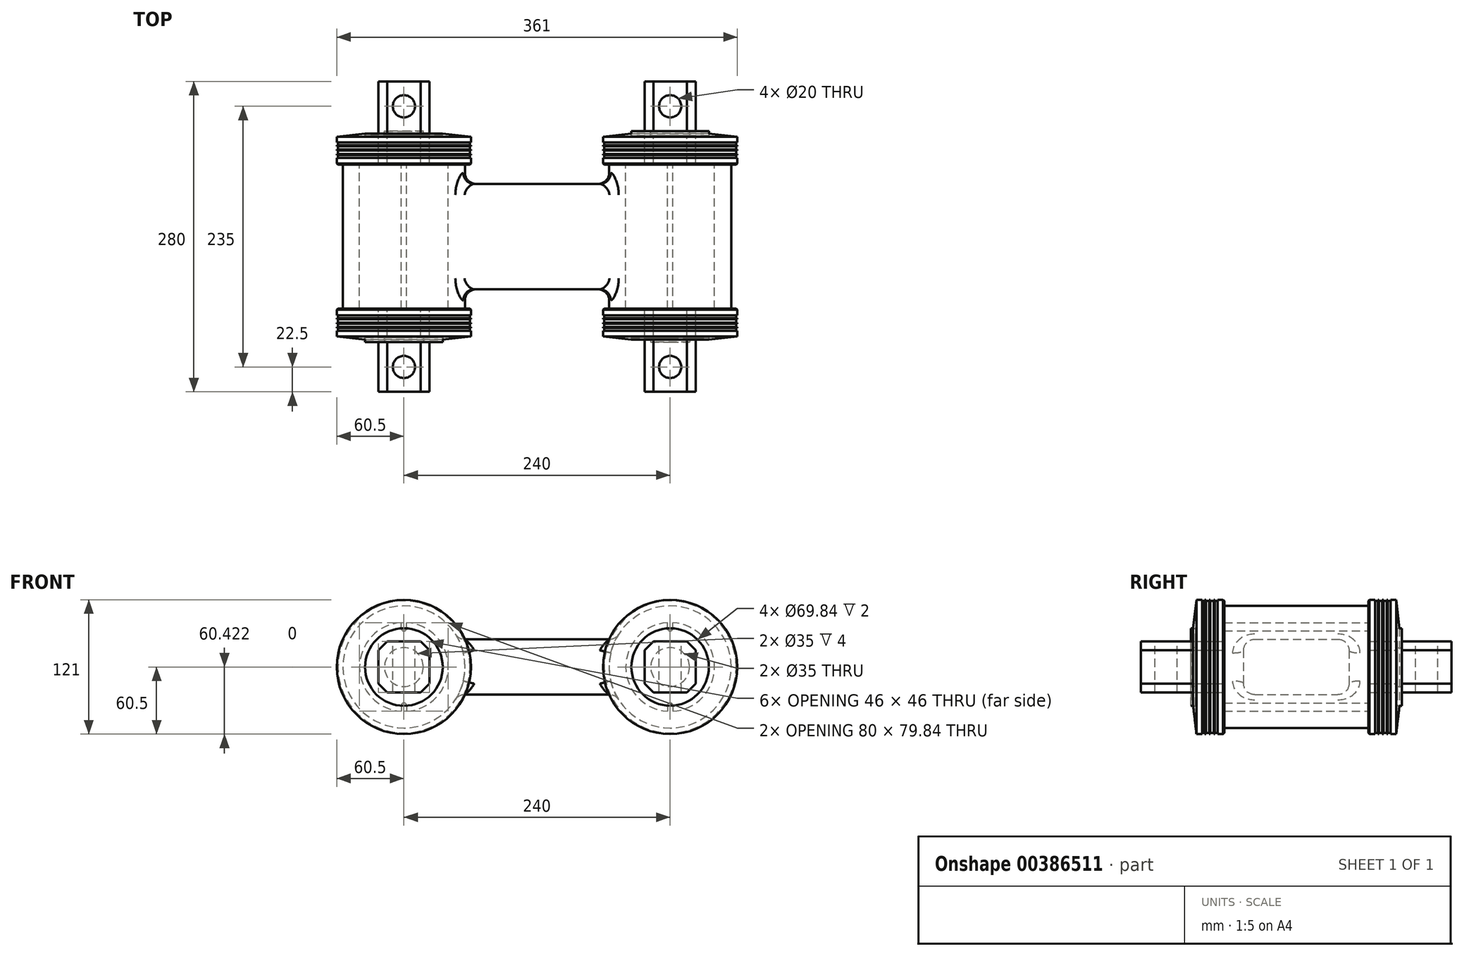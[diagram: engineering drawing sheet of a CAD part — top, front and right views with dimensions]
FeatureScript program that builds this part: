
annotation { "Feature Type Name" : "Feature", "Feature Type Description" : "" }
export const myFeature = defineFeature(function(context is Context, id is Id, definition is map)
    precondition{}
    {
        {
            var Q0;
            Q0=qCreatedBy(makeId("Front.planeOp"),FACE);
            var sketch = newSketch(context, id + "F0", { "sketchPlane" : qUnion([Q0])});
            skLineSegment(sketch, "E0", {"start": v(0, -75.22) * mm, "end": v(0, 75.8) * mm, "construction": true});
            skLineSegment(sketch, "E1.0", {"start": v(120, -75.22) * mm, "end": v(120, 75.8) * mm, "construction": true});
            skLineSegment(sketch, "E2.0", {"start": v(-120, -75.22) * mm, "end": v(-120, 75.8) * mm, "construction": true});
            skLineSegment(sketch, "E3", {"start": v(138.7, 0) * mm, "end": v(-135.83, 0) * mm, "construction": true});
            skLineSegment(sketch, "E4", {"start": v(-65.23, 25) * mm, "end": v(65.23, 25) * mm});
            skLineSegment(sketch, "E5.0", {"start": v(-65.23, -25) * mm, "end": v(65.23, -25) * mm});
            skPoint(sketch, "E6.visualSharp", {"position": v(-71.01, 25) * mm});
            skArc(sketch, "E6.filletArc", {"start": v(-73.65, 29.62) * mm, "mid": v(-70.03, 26.23) * mm, "end": v(-65.23, 25) * mm});
            skPoint(sketch, "E7.visualSharp", {"position": v(-71.01, -25) * mm});
            skArc(sketch, "E7.filletArc", {"start": v(-65.23, -25) * mm, "mid": v(-70.03, -26.23) * mm, "end": v(-73.65, -29.62) * mm});
            skPoint(sketch, "E8.visualSharp", {"position": v(71.01, 25) * mm});
            skArc(sketch, "E8.filletArc", {"start": v(65.23, 25) * mm, "mid": v(70.03, 26.23) * mm, "end": v(73.65, 29.62) * mm});
            skPoint(sketch, "E9.visualSharp", {"position": v(71.01, -25) * mm});
            skArc(sketch, "E9.filletArc", {"start": v(73.65, -29.62) * mm, "mid": v(70.03, -26.23) * mm, "end": v(65.23, -25) * mm});
            skCircle(sketch, "E10.converted", {"center": v(-120, 0) * mm, "radius": 55 * mm});
            skCircle(sketch, "E11.converted", {"center": v(120, 0) * mm, "radius": 55 * mm});
            skArc(sketch, "E12", {"start": v(-117.5, -39.92) * mm, "mid": v(-80, 0) * mm, "end": v(-117.5, 39.92) * mm});
            skArc(sketch, "E13", {"start": v(117.5, 39.92) * mm, "mid": v(80, 0) * mm, "end": v(117.5, -39.92) * mm});
            skArc(sketch, "E14", {"start": v(117.5, 35) * mm, "mid": v(120, 32.5) * mm, "end": v(122.5, 35) * mm});
            skLineSegment(sketch, "E15", {"start": v(122.5, 35) * mm, "end": v(122.5, 39.92) * mm});
            skLineSegment(sketch, "E16", {"start": v(117.5, 35) * mm, "end": v(117.5, 39.92) * mm});
            skArc(sketch, "E17.MirrorCS", {"start": v(117.5, -35) * mm, "mid": v(120, -32.5) * mm, "end": v(122.5, -35) * mm});
            skLineSegment(sketch, "E18.MirrorCS", {"start": v(122.5, -35) * mm, "end": v(122.5, -39.92) * mm});
            skLineSegment(sketch, "E19.MirrorCS", {"start": v(117.5, -35) * mm, "end": v(117.5, -39.92) * mm});
            skLineSegment(sketch, "E20.MirrorCS", {"start": v(-122.5, 35) * mm, "end": v(-122.5, 39.92) * mm});
            skLineSegment(sketch, "E21.MirrorCS", {"start": v(-117.5, 35) * mm, "end": v(-117.5, 39.92) * mm});
            skArc(sketch, "E22.MirrorCS", {"start": v(-117.5, 35) * mm, "mid": v(-120, 32.5) * mm, "end": v(-122.5, 35) * mm});
            skLineSegment(sketch, "E23.MirrorCS", {"start": v(-117.5, -35) * mm, "end": v(-117.5, -39.92) * mm});
            skArc(sketch, "E24.MirrorCS", {"start": v(-117.5, -35) * mm, "mid": v(-120, -32.5) * mm, "end": v(-122.5, -35) * mm});
            skLineSegment(sketch, "E25.MirrorCS", {"start": v(-122.5, -35) * mm, "end": v(-122.5, -39.92) * mm});
            skArc(sketch, "E26.trimOffspring", {"start": v(122.5, -39.92) * mm, "mid": v(160, 0) * mm, "end": v(122.5, 39.92) * mm});
            skArc(sketch, "E27.trimOffspring", {"start": v(-122.5, 39.92) * mm, "mid": v(-160, 0) * mm, "end": v(-122.5, -39.92) * mm});
            skSolve(sketch);
        }
        {
            var Q0;
            Q0=makeQuery(id+"F0.imprint","IMPRINT",FACE,{"disambiguationData":[TD([[makeQuery(id+"F0.imprint","IMPRINT",EDGE,{"derivedFrom":sQuery(id+"F0.wireOp",EDGE,"E12")}),-1.0]])]});
            var Q1;
            Q1=makeQuery(id+"F0.imprint","IMPRINT",FACE,{"disambiguationData":[TD([[makeQuery(id+"F0.imprint","IMPRINT",EDGE,{"derivedFrom":sQuery(id+"F0.wireOp",EDGE,"E13")}),-1.0]])]});
            extrude(context, id + "F1", {"entities" : qUnion([Q0, Q1]), "endBound" : BoundingType.SYMMETRIC, "depth" : 130 * mm});
        }
        {
            var Q0;
            Q0=makeQuery(id+"F0.imprint","IMPRINT",FACE,{"disambiguationData":[TD([[makeQuery(id+"F0.imprint","IMPRINT",EDGE,{"derivedFrom":sQuery(id+"F0.wireOp",EDGE,"E4")}),-1.0]])]});
            extrude(context, id + "F2", {"entities" : qUnion([Q0]), "operationType" : NewBodyOperationType.ADD, "endBound" : BoundingType.SYMMETRIC, "depth" : 95 * mm});
        }
        {
            var Q0;
            Q0=makeQuery(id+"F2.opExtrude","CAP_FACE",FACE,{"disambiguationData":[OSD([sQuery(id+"F0.wireOp",EDGE,"E4"),sQuery(id+"F0.wireOp",EDGE,"E5.0"),sQuery(id+"F0.wireOp",EDGE,"E6.filletArc"),sQuery(id+"F0.wireOp",EDGE,"E7.filletArc"),sQuery(id+"F0.wireOp",EDGE,"E8.filletArc"),sQuery(id+"F0.wireOp",EDGE,"E9.filletArc"),sQuery(id+"F0.wireOp",EDGE,"E10.converted"),sQuery(id+"F0.wireOp",EDGE,"E11.converted")])],"isStart":false});
            var Q1;
            Q1=makeQuery(id+"F2.opExtrude","CAP_FACE",FACE,{"disambiguationData":[OSD([sQuery(id+"F0.wireOp",EDGE,"E4"),sQuery(id+"F0.wireOp",EDGE,"E5.0"),sQuery(id+"F0.wireOp",EDGE,"E6.filletArc"),sQuery(id+"F0.wireOp",EDGE,"E7.filletArc"),sQuery(id+"F0.wireOp",EDGE,"E8.filletArc"),sQuery(id+"F0.wireOp",EDGE,"E9.filletArc"),sQuery(id+"F0.wireOp",EDGE,"E10.converted"),sQuery(id+"F0.wireOp",EDGE,"E11.converted")])],"isStart":true});
            fillet(context, id + "F3", {"entities" : qUnion([Q0, Q1]), "radius" : 10 * mm, "tangentPropagation" : true, "allowEdgeOverflow" : false});
        }
        {
            var Q0;
            Q0=qCreatedBy(makeId("Front.planeOp"),FACE);
            var sketch = newSketch(context, id + "F4", { "sketchPlane" : qUnion([Q0])});
            skArc(sketch, "E28.0", {"start": v(-117.5, -39.92) * mm, "mid": v(-80, 0) * mm, "end": v(-117.5, 39.92) * mm});
            skArc(sketch, "E28.1", {"start": v(117.5, 39.92) * mm, "mid": v(80, 0) * mm, "end": v(117.5, -39.92) * mm});
            skLineSegment(sketch, "E29.1", {"start": v(-117.5, 35) * mm, "end": v(-117.5, 39.92) * mm});
            skArc(sketch, "E29.2", {"start": v(-117.5, 35) * mm, "mid": v(-120, 32.5) * mm, "end": v(-122.5, 35) * mm});
            skLineSegment(sketch, "E29.3", {"start": v(-122.5, 35) * mm, "end": v(-122.5, 39.92) * mm});
            skArc(sketch, "E29.4", {"start": v(-122.5, 39.92) * mm, "mid": v(-160, 0) * mm, "end": v(-122.5, -39.92) * mm});
            skLineSegment(sketch, "E29.5", {"start": v(-122.5, -35) * mm, "end": v(-122.5, -39.92) * mm});
            skArc(sketch, "E29.6", {"start": v(-117.5, -35) * mm, "mid": v(-120, -32.5) * mm, "end": v(-122.5, -35) * mm});
            skLineSegment(sketch, "E29.7", {"start": v(-117.5, -35) * mm, "end": v(-117.5, -39.92) * mm});
            skLineSegment(sketch, "E30.1", {"start": v(117.5, 35) * mm, "end": v(117.5, 39.92) * mm});
            skLineSegment(sketch, "E30.2", {"start": v(122.5, 35) * mm, "end": v(122.5, 39.92) * mm});
            skArc(sketch, "E30.3", {"start": v(117.5, 35) * mm, "mid": v(120, 32.5) * mm, "end": v(122.5, 35) * mm});
            skArc(sketch, "E30.4", {"start": v(122.5, -39.92) * mm, "mid": v(160, 0) * mm, "end": v(122.5, 39.92) * mm});
            skLineSegment(sketch, "E30.5", {"start": v(122.5, -35) * mm, "end": v(122.5, -39.92) * mm});
            skArc(sketch, "E30.6", {"start": v(117.5, -35) * mm, "mid": v(120, -32.5) * mm, "end": v(122.5, -35) * mm});
            skLineSegment(sketch, "E30.7", {"start": v(117.5, -35) * mm, "end": v(117.5, -39.92) * mm});
            skSolve(sketch);
        }
        {
            var Q0;
            Q0=makeQuery(id+"F4.imprint","IMPRINT",FACE,{"disambiguationData":[TD([[makeQuery(id+"F4.imprint","IMPRINT",EDGE,{"derivedFrom":sQuery(id+"F4.wireOp",EDGE,"E28.1")}),1.0]])]});
            var Q1;
            Q1=makeQuery(id+"F4.imprint","IMPRINT",FACE,{"disambiguationData":[TD([[makeQuery(id+"F4.imprint","IMPRINT",EDGE,{"derivedFrom":sQuery(id+"F4.wireOp",EDGE,"E28.0")}),1.0]])]});
            extrude(context, id + "F5", {"entities" : qUnion([Q0, Q1]), "endBound" : BoundingType.SYMMETRIC, "depth" : 130 * mm});
        }
        {
            var Q0;
            Q0=qCreatedBy(makeId("Front.planeOp"),FACE);
            var sketch = newSketch(context, id + "F6", { "sketchPlane" : qUnion([Q0])});
            skCircle(sketch, "E31.0", {"center": v(-120, 0) * mm, "radius": 55 * mm, "construction": true});
            skCircle(sketch, "E32.0", {"center": v(120, 0) * mm, "radius": 55 * mm, "construction": true});
            skLineSegment(sketch, "E33.bottom", {"start": v(-105, -23) * mm, "end": v(-135, -23) * mm});
            skLineSegment(sketch, "E33.top", {"start": v(-105, 23) * mm, "end": v(-135, 23) * mm});
            skLineSegment(sketch, "E33.left", {"start": v(-97, -15) * mm, "end": v(-97, 15) * mm});
            skLineSegment(sketch, "E33.right", {"start": v(-143, -15) * mm, "end": v(-143, 15) * mm});
            skLineSegment(sketch, "E34", {"start": v(-120, 29.37) * mm, "end": v(-120, -29.52) * mm, "construction": true});
            skPoint(sketch, "E34.endSnap0", {"position": v(-120, 23) * mm});
            skLineSegment(sketch, "E35.0", {"start": v(-135, 29.37) * mm, "end": v(-135, -29.52) * mm, "construction": true});
            skLineSegment(sketch, "E36.0", {"start": v(-105, 29.37) * mm, "end": v(-105, -29.52) * mm, "construction": true});
            skLineSegment(sketch, "E37", {"start": v(0, 0) * mm, "end": v(0, -57.4) * mm, "construction": true});
            skLineSegment(sketch, "E38", {"start": v(-146.66, 0) * mm, "end": v(-89.7, 0) * mm, "construction": true});
            skLineSegment(sketch, "E39.0", {"start": v(-146.66, 15) * mm, "end": v(-89.7, 15) * mm, "construction": true});
            skLineSegment(sketch, "E40.0", {"start": v(-146.66, -15) * mm, "end": v(-89.7, -15) * mm, "construction": true});
            skArc(sketch, "E41.0", {"start": v(-127.46, -34.2) * mm, "mid": v(-120, -27.5) * mm, "end": v(-112.54, -34.2) * mm});
            skArc(sketch, "E41.1", {"start": v(-127.46, 34.2) * mm, "mid": v(-155, 0) * mm, "end": v(-127.46, -34.2) * mm});
            skArc(sketch, "E41.2", {"start": v(-112.54, 34.2) * mm, "mid": v(-120, 27.5) * mm, "end": v(-127.46, 34.2) * mm});
            skArc(sketch, "E41.3", {"start": v(-112.54, -34.2) * mm, "mid": v(-85, 0) * mm, "end": v(-112.54, 34.2) * mm});
            skLineSegment(sketch, "E42", {"start": v(-143, 15) * mm, "end": v(-135, 23) * mm});
            skLineSegment(sketch, "E43", {"start": v(-105, 23) * mm, "end": v(-97, 15) * mm});
            skLineSegment(sketch, "E44", {"start": v(-143, -15) * mm, "end": v(-135, -23) * mm});
            skLineSegment(sketch, "E45", {"start": v(-105, -23) * mm, "end": v(-97, -15) * mm});
            skPoint(sketch, "E46.orphan", {"position": v(-97, -23) * mm});
            skPoint(sketch, "E47.orphan", {"position": v(-97, 23) * mm});
            skPoint(sketch, "E48.orphan", {"position": v(-143, 23) * mm});
            skPoint(sketch, "E49.orphan", {"position": v(-143, -23) * mm});
            skLineSegment(sketch, "E50.MirrorCS", {"start": v(105, 23) * mm, "end": v(97, 15) * mm});
            skLineSegment(sketch, "E51.MirrorCS", {"start": v(105, -23) * mm, "end": v(97, -15) * mm});
            skLineSegment(sketch, "E52.MirrorCS", {"start": v(143, -15) * mm, "end": v(143, 15) * mm});
            skLineSegment(sketch, "E53.MirrorCS", {"start": v(105, 23) * mm, "end": v(135, 23) * mm});
            skLineSegment(sketch, "E54.MirrorCS", {"start": v(105, -23) * mm, "end": v(135, -23) * mm});
            skPoint(sketch, "E55.MirrorP", {"position": v(97, 23) * mm});
            skPoint(sketch, "E56.MirrorP", {"position": v(120, 23) * mm});
            skPoint(sketch, "E57.MirrorP", {"position": v(97, -23) * mm});
            skLineSegment(sketch, "E58.MirrorCS", {"start": v(97, -15) * mm, "end": v(97, 15) * mm});
            skLineSegment(sketch, "E59.MirrorCS", {"start": v(143, -15) * mm, "end": v(135, -23) * mm});
            skLineSegment(sketch, "E60.MirrorCS", {"start": v(143, 15) * mm, "end": v(135, 23) * mm});
            skSolve(sketch);
        }
        {
            var Q0;
            Q0=makeQuery(id+"F6.imprint","IMPRINT",FACE,{"disambiguationData":[TD([[makeQuery(id+"F6.imprint","IMPRINT",EDGE,{"derivedFrom":sQuery(id+"F6.wireOp",EDGE,"E33.bottom")}),-1.0]])]});
            extrude(context, id + "F7", {"entities" : qUnion([Q0]), "operationType" : NewBodyOperationType.ADD, "endBound" : BoundingType.SYMMETRIC, "depth" : 280 * mm});
        }
        {
            var Q0;
            Q0=makeQuery(id+"F6.imprint","IMPRINT",FACE,{"disambiguationData":[TD([[makeQuery(id+"F6.imprint","IMPRINT",EDGE,{"derivedFrom":sQuery(id+"F6.wireOp",EDGE,"E50.MirrorCS")}),1.0]])]});
            extrude(context, id + "F8", {"entities" : qUnion([Q0]), "operationType" : NewBodyOperationType.ADD, "endBound" : BoundingType.SYMMETRIC, "depth" : 280 * mm});
        }
        {
            var Q0;
            Q0=makeQuery(id+"F7.opExtrude","CAP_FACE",FACE,{"disambiguationData":[OSD([sQuery(id+"F6.wireOp",EDGE,"E33.bottom"),sQuery(id+"F6.wireOp",EDGE,"E33.top"),sQuery(id+"F6.wireOp",EDGE,"E33.left"),sQuery(id+"F6.wireOp",EDGE,"E33.right"),sQuery(id+"F6.wireOp",EDGE,"E42"),sQuery(id+"F6.wireOp",EDGE,"E43"),sQuery(id+"F6.wireOp",EDGE,"E44"),sQuery(id+"F6.wireOp",EDGE,"E45")])],"isStart":false});
            cPlane(context, id + "F9", {"entities" : qUnion([Q0]), "cplaneType" : CPlaneType.OFFSET, "offset" : 45 * mm, "oppositeDirection" : true, "width" : 150 * mm, "height" : 150 * mm});
        }
        {
            var Q0;
            Q0=qCreatedBy(id+"F9.planeOp",FACE);
            var sketch = newSketch(context, id + "F10", { "sketchPlane" : qUnion([Q0])});
            skPoint(sketch, "E61.0", {"position": v(-120, -0.08) * mm});
            skCircle(sketch, "E62", {"center": v(-120, -0.08) * mm, "radius": 35 * mm});
            skCircle(sketch, "E63", {"center": v(-120, -0.08) * mm, "radius": 17.5 * mm});
            skCircle(sketch, "E64.MirrorC", {"center": v(120, -0.08) * mm, "radius": 17.5 * mm});
            skCircle(sketch, "E65.MirrorC", {"center": v(120, -0.08) * mm, "radius": 35 * mm});
            skSolve(sketch);
        }
        {
            var Q0;
            Q0=makeQuery(id+"F10.imprint","IMPRINT",FACE,{"disambiguationData":[TD([[makeQuery(id+"F10.imprint","IMPRINT",EDGE,{"derivedFrom":sQuery(id+"F10.wireOp",EDGE,"E62")}),1.0]])]});
            extrude(context, id + "F11", {"entities" : qUnion([Q0]), "oppositeDirection" : true, "depth" : 4 * mm});
        }
        {
            var Q0;
            Q0=makeQuery(id+"F10.imprint","IMPRINT",FACE,{"disambiguationData":[TD([[makeQuery(id+"F10.imprint","IMPRINT",EDGE,{"derivedFrom":sQuery(id+"F10.wireOp",EDGE,"E64.MirrorC")}),1.0]])]});
            extrude(context, id + "F12", {"entities" : qUnion([Q0]), "oppositeDirection" : true, "depth" : 4 * mm});
        }
        {
            var Q0;
            Q0=makeQuery(id+"F8.opExtrude","CAP_FACE",FACE,{"disambiguationData":[OSD([sQuery(id+"F6.wireOp",EDGE,"E50.MirrorCS"),sQuery(id+"F6.wireOp",EDGE,"E51.MirrorCS"),sQuery(id+"F6.wireOp",EDGE,"E52.MirrorCS"),sQuery(id+"F6.wireOp",EDGE,"E53.MirrorCS"),sQuery(id+"F6.wireOp",EDGE,"E54.MirrorCS"),sQuery(id+"F6.wireOp",EDGE,"E58.MirrorCS"),sQuery(id+"F6.wireOp",EDGE,"E59.MirrorCS"),sQuery(id+"F6.wireOp",EDGE,"E60.MirrorCS")])],"isStart":true});
            cPlane(context, id + "F13", {"entities" : qUnion([Q0]), "cplaneType" : CPlaneType.OFFSET, "offset" : 45 * mm, "oppositeDirection" : true, "width" : 150 * mm, "height" : 150 * mm});
        }
        {
            var Q0;
            Q0=qCreatedBy(id+"F13.planeOp",FACE);
            var sketch = newSketch(context, id + "F14", { "sketchPlane" : qUnion([Q0])});
            skCircle(sketch, "E66.0", {"center": v(-120, -0.08) * mm, "radius": 17.5 * mm});
            skCircle(sketch, "E67.0", {"center": v(-120, -0.08) * mm, "radius": 35 * mm});
            skCircle(sketch, "E68.0", {"center": v(120, -0.08) * mm, "radius": 17.5 * mm});
            skCircle(sketch, "E69.0", {"center": v(120, -0.08) * mm, "radius": 35 * mm});
            skSolve(sketch);
        }
        {
            var Q0;
            Q0=makeQuery(id+"F14.imprint","IMPRINT",FACE,{"disambiguationData":[TD([[makeQuery(id+"F14.imprint","IMPRINT",EDGE,{"derivedFrom":sQuery(id+"F14.wireOp",EDGE,"E66.0")}),-1.0]])]});
            var Q1;
            Q1=makeQuery(id+"F14.imprint","IMPRINT",FACE,{"disambiguationData":[TD([[makeQuery(id+"F14.imprint","IMPRINT",EDGE,{"derivedFrom":sQuery(id+"F14.wireOp",EDGE,"E68.0")}),1.0]])]});
            extrude(context, id + "F15", {"entities" : qUnion([Q0, Q1]), "oppositeDirection" : true, "depth" : 4 * mm});
        }
        {
            var Q0;
            Q0=makeQuery(id+"F12.opExtrude","SWEPT_BODY",BODY,{"disambiguationData":[OSD([sQuery(id+"F10.wireOp",EDGE,"E64.MirrorC"),sQuery(id+"F10.wireOp",EDGE,"E65.MirrorC")])]});
            var Q1;
            Q1=makeQuery(id+"F15.opExtrude","SWEPT_BODY",BODY,{"disambiguationData":[OSD([sQuery(id+"F14.wireOp",EDGE,"E66.0"),sQuery(id+"F14.wireOp",EDGE,"E67.0")])]});
            var Q2;
            Q2=makeQuery(id+"F5.opExtrude","SWEPT_BODY",BODY,{"disambiguationData":[OSD([sQuery(id+"F4.wireOp",EDGE,"E28.1"),sQuery(id+"F4.wireOp",EDGE,"E30.1"),sQuery(id+"F4.wireOp",EDGE,"E30.2"),sQuery(id+"F4.wireOp",EDGE,"E30.3"),sQuery(id+"F4.wireOp",EDGE,"E30.4"),sQuery(id+"F4.wireOp",EDGE,"E30.5"),sQuery(id+"F4.wireOp",EDGE,"E30.6"),sQuery(id+"F4.wireOp",EDGE,"E30.7")])]});
            booleanBodies(context, id + "F16", {"operationType" : BooleanOperationType.SUBTRACTION, "tools" : qUnion([Q0, Q1]), "targets" : qUnion([Q2]), "keepTools" : true});
        }
        {
            var Q0;
            Q0=makeQuery(id+"F15.opExtrude","SWEPT_BODY",BODY,{"disambiguationData":[OSD([sQuery(id+"F14.wireOp",EDGE,"E68.0"),sQuery(id+"F14.wireOp",EDGE,"E69.0")])]});
            var Q1;
            Q1=makeQuery(id+"F11.opExtrude","SWEPT_BODY",BODY,{"disambiguationData":[OSD([sQuery(id+"F10.wireOp",EDGE,"E62"),sQuery(id+"F10.wireOp",EDGE,"E63")])]});
            var Q2;
            Q2=makeQuery(id+"F5.opExtrude","SWEPT_BODY",BODY,{"disambiguationData":[OSD([sQuery(id+"F4.wireOp",EDGE,"E28.0"),sQuery(id+"F4.wireOp",EDGE,"E29.1"),sQuery(id+"F4.wireOp",EDGE,"E29.2"),sQuery(id+"F4.wireOp",EDGE,"E29.3"),sQuery(id+"F4.wireOp",EDGE,"E29.4"),sQuery(id+"F4.wireOp",EDGE,"E29.5"),sQuery(id+"F4.wireOp",EDGE,"E29.6"),sQuery(id+"F4.wireOp",EDGE,"E29.7")])]});
            booleanBodies(context, id + "F17", {"operationType" : BooleanOperationType.SUBTRACTION, "tools" : qUnion([Q0, Q1]), "targets" : qUnion([Q2]), "keepTools" : true});
        }
        {
            var Q0;
            Q0=qCreatedBy(makeId("Top.planeOp"),FACE);
            var sketch = newSketch(context, id + "F18", { "sketchPlane" : qUnion([Q0])});
            skPoint(sketch, "E70.0", {"position": v(-120, -140) * mm});
            skPoint(sketch, "E71.0", {"position": v(-120, 140) * mm});
            skPoint(sketch, "E72.0", {"position": v(120, 140) * mm});
            skPoint(sketch, "E73.0", {"position": v(120, -140) * mm});
            skCircle(sketch, "E74", {"center": v(-120, 117.5) * mm, "radius": 10 * mm});
            skCircle(sketch, "E75.MirrorC", {"center": v(-120, -117.5) * mm, "radius": 10 * mm});
            skCircle(sketch, "E76.MirrorC", {"center": v(120, 117.5) * mm, "radius": 10 * mm});
            skCircle(sketch, "E77.MirrorC", {"center": v(120, -117.5) * mm, "radius": 10 * mm});
            skSolve(sketch);
        }
        {
            var Q0;
            Q0 = qSketchRegion(id + "F18", true);
            var Q1;
            Q1=sQuery(id+"F18.wireOp",EDGE,"E74");
            var Q2;
            Q2=sQuery(id+"F18.wireOp",EDGE,"E76.MirrorC");
            var Q3;
            Q3=sQuery(id+"F18.wireOp",EDGE,"E77.MirrorC");
            var Q4;
            Q4=sQuery(id+"F18.wireOp",EDGE,"E75.MirrorC");
            extrude(context, id + "F19", {"entities" : qUnion([Q0]), "operationType" : NewBodyOperationType.REMOVE, "surfaceEntities" : qUnion([Q1, Q2, Q3, Q4]), "endBound" : BoundingType.SYMMETRIC, "oppositeDirection" : true, "depth" : 100 * mm});
        }
        {
            var Q0;
            {var subQ2=sQuery(id+"F6.wireOp",EDGE,"E33.right");Q0=makeQuery(id+"F17.opBoolean","SPLIT",FACE,{"disambiguationData":[TD([makeQuery(id+"F15.opExtrude","CAP_FACE",FACE,{"disambiguationData":[OSD([sQuery(id+"F14.wireOp",EDGE,"E68.0"),sQuery(id+"F14.wireOp",EDGE,"E69.0")])],"isStart":true})])],"derivedFrom":makeQuery(id+"F7.boolean.opBoolean","SPLIT",FACE,{"disambiguationData":[TD([makeQuery(id+"F5.opExtrude","CAP_FACE",FACE,{"disambiguationData":[OSD([sQuery(id+"F4.wireOp",EDGE,"E28.0"),sQuery(id+"F4.wireOp",EDGE,"E29.1"),sQuery(id+"F4.wireOp",EDGE,"E29.2"),sQuery(id+"F4.wireOp",EDGE,"E29.3"),sQuery(id+"F4.wireOp",EDGE,"E29.4"),sQuery(id+"F4.wireOp",EDGE,"E29.5"),sQuery(id+"F4.wireOp",EDGE,"E29.6"),sQuery(id+"F4.wireOp",EDGE,"E29.7")])],"isStart":true})])],"derivedFrom":makeQuery(id+"F7.opExtrude","SWEPT_FACE",FACE,{"disambiguationData":[OSD([subQ2])]})})});}
            var Q1;
            {var subQ2=sQuery(id+"F6.wireOp",EDGE,"E33.left");Q1=makeQuery(id+"F17.opBoolean","SPLIT",FACE,{"disambiguationData":[TD([makeQuery(id+"F11.opExtrude","CAP_FACE",FACE,{"disambiguationData":[OSD([sQuery(id+"F10.wireOp",EDGE,"E62"),sQuery(id+"F10.wireOp",EDGE,"E63")])],"isStart":true})])],"derivedFrom":makeQuery(id+"F7.boolean.opBoolean","SPLIT",FACE,{"disambiguationData":[TD([makeQuery(id+"F5.opExtrude","CAP_FACE",FACE,{"disambiguationData":[OSD([sQuery(id+"F4.wireOp",EDGE,"E28.0"),sQuery(id+"F4.wireOp",EDGE,"E29.1"),sQuery(id+"F4.wireOp",EDGE,"E29.2"),sQuery(id+"F4.wireOp",EDGE,"E29.3"),sQuery(id+"F4.wireOp",EDGE,"E29.4"),sQuery(id+"F4.wireOp",EDGE,"E29.5"),sQuery(id+"F4.wireOp",EDGE,"E29.6"),sQuery(id+"F4.wireOp",EDGE,"E29.7")])],"isStart":false})])],"derivedFrom":makeQuery(id+"F7.opExtrude","SWEPT_FACE",FACE,{"disambiguationData":[OSD([subQ2])]})})});}
            cPlane(context, id + "F20", {"entities" : qUnion([Q0, Q1]), "cplaneType" : CPlaneType.MID_PLANE, "offset" : 25 * mm, "width" : 150 * mm, "height" : 150 * mm});
        }
        {
            var Q0;
            Q0=qCreatedBy(id+"F20.planeOp",FACE);
            var sketch = newSketch(context, id + "F21", { "sketchPlane" : qUnion([Q0])});
            skPoint(sketch, "E78.0", {"position": v(-140, 0) * mm});
            skPoint(sketch, "E79.0", {"position": v(140, 0) * mm});
            skLineSegment(sketch, "E80", {"start": v(-140, 0) * mm, "end": v(140, 0) * mm, "construction": true});
            skLineSegment(sketch, "E81.0", {"start": v(-91, 60.5) * mm, "end": v(-91, -35.08) * mm, "construction": true});
            skPoint(sketch, "E82.orphan", {"position": v(-91, 34.92) * mm});
            skPoint(sketch, "E83.orphan", {"position": v(91, 34.92) * mm});
            skLineSegment(sketch, "E84.0", {"start": v(-65, 60.5) * mm, "end": v(-65, -55) * mm, "construction": true});
            skPoint(sketch, "E85.orphan", {"position": v(-65, 55) * mm});
            skPoint(sketch, "E86.orphan", {"position": v(65, 55) * mm});
            skLineSegment(sketch, "E87.0", {"start": v(-93, 60.5) * mm, "end": v(-93, -35.08) * mm, "construction": true});
            skLineSegment(sketch, "E88.0", {"start": v(-90, 60.5) * mm, "end": v(-90, -35.08) * mm, "construction": true});
            skLineSegment(sketch, "E89.0", {"start": v(-85, 60.5) * mm, "end": v(-85, -35.08) * mm, "construction": true});
            skLineSegment(sketch, "E90.0", {"start": v(-66, 60.5) * mm, "end": v(-66, -55) * mm, "construction": true});
            skLineSegment(sketch, "E91.0", {"start": v(-71, 60.5) * mm, "end": v(-71, -55) * mm, "construction": true});
            skLineSegment(sketch, "E92.0", {"start": v(-82.5, 60.5) * mm, "end": v(-82.5, -35.08) * mm, "construction": true});
            skLineSegment(sketch, "E93.0", {"start": v(-81.5, 60.5) * mm, "end": v(-81.5, -35.08) * mm, "construction": true});
            skLineSegment(sketch, "E94.0", {"start": v(-78.5, 60.5) * mm, "end": v(-78.5, -35.08) * mm, "construction": true});
            skLineSegment(sketch, "E95.0", {"start": v(-77.5, 60.5) * mm, "end": v(-77.5, -35.08) * mm, "construction": true});
            skLineSegment(sketch, "E96.0", {"start": v(-74.5, 60.5) * mm, "end": v(-74.5, -35.08) * mm, "construction": true});
            skLineSegment(sketch, "E97.0", {"start": v(-73.5, 60.5) * mm, "end": v(-73.5, -35.08) * mm, "construction": true});
            skLineSegment(sketch, "E98.0", {"start": v(-140, 39.5) * mm, "end": v(140, 39.5) * mm, "construction": true});
            skLineSegment(sketch, "E99", {"start": v(-90, 60.5) * mm, "end": v(-85, 60.5) * mm});
            skLineSegment(sketch, "E100", {"start": v(-85, 59.5) * mm, "end": v(-82.5, 59.5) * mm});
            skLineSegment(sketch, "E101", {"start": v(-82.5, 59.5) * mm, "end": v(-82.5, 60.5) * mm});
            skLineSegment(sketch, "E102", {"start": v(-81.5, 60.5) * mm, "end": v(-81.5, 59.5) * mm});
            skLineSegment(sketch, "E103", {"start": v(-81.5, 59.5) * mm, "end": v(-78.5, 59.5) * mm});
            skLineSegment(sketch, "E104", {"start": v(-78.5, 59.5) * mm, "end": v(-78.5, 60.5) * mm});
            skLineSegment(sketch, "E105", {"start": v(-77.5, 60.5) * mm, "end": v(-77.5, 59.5) * mm});
            skLineSegment(sketch, "E106", {"start": v(-77.5, 59.5) * mm, "end": v(-74.5, 59.5) * mm});
            skLineSegment(sketch, "E107", {"start": v(-74.5, 59.5) * mm, "end": v(-74.5, 60.5) * mm});
            skLineSegment(sketch, "E108", {"start": v(-73.5, 60.5) * mm, "end": v(-73.5, 59.5) * mm});
            skLineSegment(sketch, "E109", {"start": v(-73.5, 59.5) * mm, "end": v(-71, 59.5) * mm});
            skLineSegment(sketch, "E110", {"start": v(-71, 59.5) * mm, "end": v(-71, 60.5) * mm});
            skLineSegment(sketch, "E111", {"start": v(-66, 60.5) * mm, "end": v(-65, 59.5) * mm});
            skLineSegment(sketch, "E112", {"start": v(-65, 59.5) * mm, "end": v(-65, 0) * mm});
            skLineSegment(sketch, "E113", {"start": v(-65, 0) * mm, "end": v(-91, 0) * mm});
            skLineSegment(sketch, "E114", {"start": v(-91, 0) * mm, "end": v(-91, 34.92) * mm});
            skLineSegment(sketch, "E115", {"start": v(-85, 60.5) * mm, "end": v(-85, 59.5) * mm});
            skLineSegment(sketch, "E116", {"start": v(-82.5, 60.5) * mm, "end": v(-81.5, 60.5) * mm});
            skLineSegment(sketch, "E117", {"start": v(-78.5, 60.5) * mm, "end": v(-77.5, 60.5) * mm});
            skLineSegment(sketch, "E118", {"start": v(-74.5, 60.5) * mm, "end": v(-73.5, 60.5) * mm});
            skLineSegment(sketch, "E119", {"start": v(-71, 60.5) * mm, "end": v(-66, 60.5) * mm});
            skLineSegment(sketch, "E120", {"start": v(-95, 34.92) * mm, "end": v(-91, 34.92) * mm, "construction": true});
            skLineSegment(sketch, "E121", {"start": v(-91, 34.92) * mm, "end": v(-93, 34.92) * mm});
            skLineSegment(sketch, "E122", {"start": v(-93, 34.92) * mm, "end": v(-90, 60.5) * mm});
            skLineSegment(sketch, "E123.MirrorCS", {"start": v(74.5, 59.5) * mm, "end": v(74.5, 60.5) * mm});
            skLineSegment(sketch, "E124.MirrorCS", {"start": v(73.5, 60.5) * mm, "end": v(73.5, 59.5) * mm});
            skLineSegment(sketch, "E125.MirrorCS", {"start": v(74.5, 60.5) * mm, "end": v(73.5, 60.5) * mm});
            skLineSegment(sketch, "E126.MirrorCS", {"start": v(78.5, 59.5) * mm, "end": v(78.5, 60.5) * mm});
            skLineSegment(sketch, "E127.MirrorCS", {"start": v(81.5, 59.5) * mm, "end": v(78.5, 59.5) * mm});
            skLineSegment(sketch, "E128.MirrorCS", {"start": v(77.5, 60.5) * mm, "end": v(77.5, 59.5) * mm});
            skLineSegment(sketch, "E129.MirrorCS", {"start": v(82.5, 59.5) * mm, "end": v(82.5, 60.5) * mm});
            skLineSegment(sketch, "E130.MirrorCS", {"start": v(78.5, 60.5) * mm, "end": v(77.5, 60.5) * mm});
            skLineSegment(sketch, "E131.MirrorCS", {"start": v(81.5, 60.5) * mm, "end": v(81.5, 59.5) * mm});
            skLineSegment(sketch, "E132.MirrorCS", {"start": v(82.5, 60.5) * mm, "end": v(81.5, 60.5) * mm});
            skLineSegment(sketch, "E133.MirrorCS", {"start": v(77.5, 59.5) * mm, "end": v(74.5, 59.5) * mm});
            skLineSegment(sketch, "E134.MirrorCS", {"start": v(85, 60.5) * mm, "end": v(85, 59.5) * mm});
            skLineSegment(sketch, "E135.MirrorCS", {"start": v(71, 59.5) * mm, "end": v(71, 60.5) * mm});
            skLineSegment(sketch, "E136.MirrorCS", {"start": v(73.5, 59.5) * mm, "end": v(71, 59.5) * mm});
            skLineSegment(sketch, "E137.MirrorCS", {"start": v(85, 59.5) * mm, "end": v(82.5, 59.5) * mm});
            skLineSegment(sketch, "E138.MirrorCS", {"start": v(66, 60.5) * mm, "end": v(65, 59.5) * mm});
            skLineSegment(sketch, "E139.MirrorCS", {"start": v(91, 34.92) * mm, "end": v(93, 34.92) * mm});
            skLineSegment(sketch, "E140.MirrorCS", {"start": v(95, 34.92) * mm, "end": v(91, 34.92) * mm, "construction": true});
            skLineSegment(sketch, "E141.MirrorCS", {"start": v(91, 0) * mm, "end": v(91, 34.92) * mm});
            skLineSegment(sketch, "E142.MirrorCS", {"start": v(71, 60.5) * mm, "end": v(66, 60.5) * mm});
            skLineSegment(sketch, "E143.MirrorCS", {"start": v(90, 60.5) * mm, "end": v(85, 60.5) * mm});
            skLineSegment(sketch, "E144.MirrorCS", {"start": v(65, 0) * mm, "end": v(91, 0) * mm});
            skLineSegment(sketch, "E145.MirrorCS", {"start": v(65, 59.5) * mm, "end": v(65, 0) * mm});
            skLineSegment(sketch, "E146.MirrorCS", {"start": v(93, 34.92) * mm, "end": v(90, 60.5) * mm});
            skSolve(sketch);
        }
        {
            var Q0;
            Q0 = qSketchRegion(id + "F21", true);
            var Q1;
            Q1=sQuery(id+"F21.wireOp",EDGE,"E80");
            revolve(context, id + "F22", {"entities" : qUnion([Q0]), "axis" : qUnion([Q1]), "revolveType" : RevolveType.FULL});
        }
        {
            var Q0;
            Q0=makeQuery(id+"F5.opExtrude","SWEPT_BODY",BODY,{"disambiguationData":[OSD([sQuery(id+"F4.wireOp",EDGE,"E28.0"),sQuery(id+"F4.wireOp",EDGE,"E29.1"),sQuery(id+"F4.wireOp",EDGE,"E29.2"),sQuery(id+"F4.wireOp",EDGE,"E29.3"),sQuery(id+"F4.wireOp",EDGE,"E29.4"),sQuery(id+"F4.wireOp",EDGE,"E29.5"),sQuery(id+"F4.wireOp",EDGE,"E29.6"),sQuery(id+"F4.wireOp",EDGE,"E29.7")])]});
            var Q1;
            Q1=makeQuery(id+"F22.opRevolve","SWEPT_BODY",BODY,{"disambiguationData":[OSD([sQuery(id+"F21.wireOp",EDGE,"E99"),sQuery(id+"F21.wireOp",EDGE,"E100"),sQuery(id+"F21.wireOp",EDGE,"E101"),sQuery(id+"F21.wireOp",EDGE,"E102"),sQuery(id+"F21.wireOp",EDGE,"E103"),sQuery(id+"F21.wireOp",EDGE,"E104"),sQuery(id+"F21.wireOp",EDGE,"E105"),sQuery(id+"F21.wireOp",EDGE,"E106"),sQuery(id+"F21.wireOp",EDGE,"E107"),sQuery(id+"F21.wireOp",EDGE,"E108"),sQuery(id+"F21.wireOp",EDGE,"E109"),sQuery(id+"F21.wireOp",EDGE,"E110"),sQuery(id+"F21.wireOp",EDGE,"E111"),sQuery(id+"F21.wireOp",EDGE,"E112"),sQuery(id+"F21.wireOp",EDGE,"E113"),sQuery(id+"F21.wireOp",EDGE,"E114"),sQuery(id+"F21.wireOp",EDGE,"E115"),sQuery(id+"F21.wireOp",EDGE,"E116"),sQuery(id+"F21.wireOp",EDGE,"E117"),sQuery(id+"F21.wireOp",EDGE,"E118"),sQuery(id+"F21.wireOp",EDGE,"E119"),sQuery(id+"F21.wireOp",EDGE,"E121"),sQuery(id+"F21.wireOp",EDGE,"E122")])]});
            var Q2;
            Q2=makeQuery(id+"F22.opRevolve","SWEPT_BODY",BODY,{"disambiguationData":[OSD([sQuery(id+"F21.wireOp",EDGE,"E123.MirrorCS"),sQuery(id+"F21.wireOp",EDGE,"E124.MirrorCS"),sQuery(id+"F21.wireOp",EDGE,"E125.MirrorCS"),sQuery(id+"F21.wireOp",EDGE,"E126.MirrorCS"),sQuery(id+"F21.wireOp",EDGE,"E127.MirrorCS"),sQuery(id+"F21.wireOp",EDGE,"E128.MirrorCS"),sQuery(id+"F21.wireOp",EDGE,"E129.MirrorCS"),sQuery(id+"F21.wireOp",EDGE,"E130.MirrorCS"),sQuery(id+"F21.wireOp",EDGE,"E131.MirrorCS"),sQuery(id+"F21.wireOp",EDGE,"E132.MirrorCS"),sQuery(id+"F21.wireOp",EDGE,"E133.MirrorCS"),sQuery(id+"F21.wireOp",EDGE,"E134.MirrorCS"),sQuery(id+"F21.wireOp",EDGE,"E135.MirrorCS"),sQuery(id+"F21.wireOp",EDGE,"E136.MirrorCS"),sQuery(id+"F21.wireOp",EDGE,"E137.MirrorCS"),sQuery(id+"F21.wireOp",EDGE,"E138.MirrorCS"),sQuery(id+"F21.wireOp",EDGE,"E139.MirrorCS"),sQuery(id+"F21.wireOp",EDGE,"E141.MirrorCS"),sQuery(id+"F21.wireOp",EDGE,"E142.MirrorCS"),sQuery(id+"F21.wireOp",EDGE,"E143.MirrorCS"),sQuery(id+"F21.wireOp",EDGE,"E144.MirrorCS"),sQuery(id+"F21.wireOp",EDGE,"E145.MirrorCS"),sQuery(id+"F21.wireOp",EDGE,"E146.MirrorCS")])]});
            booleanBodies(context, id + "F23", {"operationType" : BooleanOperationType.SUBTRACTION, "tools" : qUnion([Q0]), "targets" : qUnion([Q1, Q2]), "keepTools" : true});
        }
        {
            var Q0;
            {var subQ2=sQuery(id+"F6.wireOp",EDGE,"E52.MirrorCS");Q0=makeQuery(id+"F16.opBoolean","SPLIT",FACE,{"disambiguationData":[TD([makeQuery(id+"F12.opExtrude","CAP_FACE",FACE,{"disambiguationData":[OSD([sQuery(id+"F10.wireOp",EDGE,"E64.MirrorC"),sQuery(id+"F10.wireOp",EDGE,"E65.MirrorC")])],"isStart":true})])],"derivedFrom":makeQuery(id+"F8.boolean.opBoolean","SPLIT",FACE,{"disambiguationData":[TD([makeQuery(id+"F5.opExtrude","CAP_FACE",FACE,{"disambiguationData":[OSD([sQuery(id+"F4.wireOp",EDGE,"E28.1"),sQuery(id+"F4.wireOp",EDGE,"E30.1"),sQuery(id+"F4.wireOp",EDGE,"E30.2"),sQuery(id+"F4.wireOp",EDGE,"E30.3"),sQuery(id+"F4.wireOp",EDGE,"E30.4"),sQuery(id+"F4.wireOp",EDGE,"E30.5"),sQuery(id+"F4.wireOp",EDGE,"E30.6"),sQuery(id+"F4.wireOp",EDGE,"E30.7")])],"isStart":false})])],"derivedFrom":makeQuery(id+"F8.opExtrude","SWEPT_FACE",FACE,{"disambiguationData":[OSD([subQ2])]})})});}
            var Q1;
            {var subQ2=sQuery(id+"F6.wireOp",EDGE,"E58.MirrorCS");Q1=makeQuery(id+"F16.opBoolean","SPLIT",FACE,{"disambiguationData":[TD([makeQuery(id+"F15.opExtrude","CAP_FACE",FACE,{"disambiguationData":[OSD([sQuery(id+"F14.wireOp",EDGE,"E66.0"),sQuery(id+"F14.wireOp",EDGE,"E67.0")])],"isStart":true})])],"derivedFrom":makeQuery(id+"F8.boolean.opBoolean","SPLIT",FACE,{"disambiguationData":[TD([makeQuery(id+"F5.opExtrude","CAP_FACE",FACE,{"disambiguationData":[OSD([sQuery(id+"F4.wireOp",EDGE,"E28.1"),sQuery(id+"F4.wireOp",EDGE,"E30.1"),sQuery(id+"F4.wireOp",EDGE,"E30.2"),sQuery(id+"F4.wireOp",EDGE,"E30.3"),sQuery(id+"F4.wireOp",EDGE,"E30.4"),sQuery(id+"F4.wireOp",EDGE,"E30.5"),sQuery(id+"F4.wireOp",EDGE,"E30.6"),sQuery(id+"F4.wireOp",EDGE,"E30.7")])],"isStart":true})])],"derivedFrom":makeQuery(id+"F8.opExtrude","SWEPT_FACE",FACE,{"disambiguationData":[OSD([subQ2])]})})});}
            cPlane(context, id + "F24", {"entities" : qUnion([Q0, Q1]), "cplaneType" : CPlaneType.MID_PLANE, "offset" : 25 * mm, "width" : 150 * mm, "height" : 150 * mm});
        }
        {
            var Q0;
            Q0=qCreatedBy(id+"F24.planeOp",FACE);
            var sketch = newSketch(context, id + "F25", { "sketchPlane" : qUnion([Q0])});
            skPoint(sketch, "E147.0", {"position": v(-127.7, -41.34) * mm});
            skPoint(sketch, "E148.0", {"position": v(152.3, -41.34) * mm});
            skLineSegment(sketch, "E149", {"start": v(-140, 0) * mm, "end": v(140, 0) * mm, "construction": true});
            skLineSegment(sketch, "E150.0", {"start": v(-91, 60.5) * mm, "end": v(-91, -35.08) * mm, "construction": true});
            skPoint(sketch, "E151.orphan", {"position": v(-91, 34.92) * mm});
            skPoint(sketch, "E152.orphan", {"position": v(91, 34.92) * mm});
            skLineSegment(sketch, "E153.0", {"start": v(-65, 60.5) * mm, "end": v(-65, -55) * mm, "construction": true});
            skPoint(sketch, "E154.orphan", {"position": v(-65, 55) * mm});
            skPoint(sketch, "E155.orphan", {"position": v(65, 55) * mm});
            skLineSegment(sketch, "E156.0", {"start": v(-93, 60.5) * mm, "end": v(-93, -35.08) * mm, "construction": true});
            skLineSegment(sketch, "E157.0", {"start": v(-90, 60.5) * mm, "end": v(-90, -35.08) * mm, "construction": true});
            skLineSegment(sketch, "E158.0", {"start": v(-85, 60.5) * mm, "end": v(-85, -35.08) * mm, "construction": true});
            skLineSegment(sketch, "E159.0", {"start": v(-66, 60.5) * mm, "end": v(-66, -55) * mm, "construction": true});
            skLineSegment(sketch, "E160.0", {"start": v(-71, 60.5) * mm, "end": v(-71, -55) * mm, "construction": true});
            skLineSegment(sketch, "E161.0", {"start": v(-82.5, 60.5) * mm, "end": v(-82.5, -35.08) * mm, "construction": true});
            skLineSegment(sketch, "E162.0", {"start": v(-81.5, 60.5) * mm, "end": v(-81.5, -35.08) * mm, "construction": true});
            skLineSegment(sketch, "E163.0", {"start": v(-78.5, 60.5) * mm, "end": v(-78.5, -35.08) * mm, "construction": true});
            skLineSegment(sketch, "E164.0", {"start": v(-77.5, 60.5) * mm, "end": v(-77.5, -35.08) * mm, "construction": true});
            skLineSegment(sketch, "E165.0", {"start": v(-74.5, 60.5) * mm, "end": v(-74.5, -35.08) * mm, "construction": true});
            skLineSegment(sketch, "E166.0", {"start": v(-73.5, 60.5) * mm, "end": v(-73.5, -35.08) * mm, "construction": true});
            skLineSegment(sketch, "E167.0", {"start": v(-140, 39.5) * mm, "end": v(140, 39.5) * mm, "construction": true});
            skLineSegment(sketch, "E168", {"start": v(-90, 60.5) * mm, "end": v(-85, 60.5) * mm});
            skLineSegment(sketch, "E169", {"start": v(-85, 59.5) * mm, "end": v(-82.5, 59.5) * mm});
            skLineSegment(sketch, "E170", {"start": v(-82.5, 59.5) * mm, "end": v(-82.5, 60.5) * mm});
            skLineSegment(sketch, "E171", {"start": v(-81.5, 60.5) * mm, "end": v(-81.5, 59.5) * mm});
            skLineSegment(sketch, "E172", {"start": v(-81.5, 59.5) * mm, "end": v(-78.5, 59.5) * mm});
            skLineSegment(sketch, "E173", {"start": v(-78.5, 59.5) * mm, "end": v(-78.5, 60.5) * mm});
            skLineSegment(sketch, "E174", {"start": v(-77.5, 60.5) * mm, "end": v(-77.5, 59.5) * mm});
            skLineSegment(sketch, "E175", {"start": v(-77.5, 59.5) * mm, "end": v(-74.5, 59.5) * mm});
            skLineSegment(sketch, "E176", {"start": v(-74.5, 59.5) * mm, "end": v(-74.5, 60.5) * mm});
            skLineSegment(sketch, "E177", {"start": v(-73.5, 60.5) * mm, "end": v(-73.5, 59.5) * mm});
            skLineSegment(sketch, "E178", {"start": v(-73.5, 59.5) * mm, "end": v(-71, 59.5) * mm});
            skLineSegment(sketch, "E179", {"start": v(-71, 59.5) * mm, "end": v(-71, 60.5) * mm});
            skLineSegment(sketch, "E180", {"start": v(-66, 60.5) * mm, "end": v(-65, 59.5) * mm});
            skLineSegment(sketch, "E181", {"start": v(-65, 59.5) * mm, "end": v(-65, 0) * mm});
            skLineSegment(sketch, "E182", {"start": v(-65, 0) * mm, "end": v(-91, 0) * mm});
            skLineSegment(sketch, "E183", {"start": v(-91, 0) * mm, "end": v(-91, 34.92) * mm});
            skLineSegment(sketch, "E184", {"start": v(-85, 60.5) * mm, "end": v(-85, 59.5) * mm});
            skLineSegment(sketch, "E185", {"start": v(-82.5, 60.5) * mm, "end": v(-81.5, 60.5) * mm});
            skLineSegment(sketch, "E186", {"start": v(-78.5, 60.5) * mm, "end": v(-77.5, 60.5) * mm});
            skLineSegment(sketch, "E187", {"start": v(-74.5, 60.5) * mm, "end": v(-73.5, 60.5) * mm});
            skLineSegment(sketch, "E188", {"start": v(-71, 60.5) * mm, "end": v(-66, 60.5) * mm});
            skLineSegment(sketch, "E189", {"start": v(-95, 34.92) * mm, "end": v(-91, 34.92) * mm, "construction": true});
            skLineSegment(sketch, "E190", {"start": v(-91, 34.92) * mm, "end": v(-93, 34.92) * mm});
            skLineSegment(sketch, "E191", {"start": v(-93, 34.92) * mm, "end": v(-90, 60.5) * mm});
            skLineSegment(sketch, "E192.MirrorCS", {"start": v(74.5, 59.5) * mm, "end": v(74.5, 60.5) * mm});
            skLineSegment(sketch, "E193.MirrorCS", {"start": v(73.5, 60.5) * mm, "end": v(73.5, 59.5) * mm});
            skLineSegment(sketch, "E194.MirrorCS", {"start": v(74.5, 60.5) * mm, "end": v(73.5, 60.5) * mm});
            skLineSegment(sketch, "E195.MirrorCS", {"start": v(78.5, 59.5) * mm, "end": v(78.5, 60.5) * mm});
            skLineSegment(sketch, "E196.MirrorCS", {"start": v(81.5, 59.5) * mm, "end": v(78.5, 59.5) * mm});
            skLineSegment(sketch, "E197.MirrorCS", {"start": v(77.5, 60.5) * mm, "end": v(77.5, 59.5) * mm});
            skLineSegment(sketch, "E198.MirrorCS", {"start": v(82.5, 59.5) * mm, "end": v(82.5, 60.5) * mm});
            skLineSegment(sketch, "E199.MirrorCS", {"start": v(78.5, 60.5) * mm, "end": v(77.5, 60.5) * mm});
            skLineSegment(sketch, "E200.MirrorCS", {"start": v(81.5, 60.5) * mm, "end": v(81.5, 59.5) * mm});
            skLineSegment(sketch, "E201.MirrorCS", {"start": v(82.5, 60.5) * mm, "end": v(81.5, 60.5) * mm});
            skLineSegment(sketch, "E202.MirrorCS", {"start": v(77.5, 59.5) * mm, "end": v(74.5, 59.5) * mm});
            skLineSegment(sketch, "E203.MirrorCS", {"start": v(85, 60.5) * mm, "end": v(85, 59.5) * mm});
            skLineSegment(sketch, "E204.MirrorCS", {"start": v(71, 59.5) * mm, "end": v(71, 60.5) * mm});
            skLineSegment(sketch, "E205.MirrorCS", {"start": v(73.5, 59.5) * mm, "end": v(71, 59.5) * mm});
            skLineSegment(sketch, "E206.MirrorCS", {"start": v(85, 59.5) * mm, "end": v(82.5, 59.5) * mm});
            skLineSegment(sketch, "E207.MirrorCS", {"start": v(66, 60.5) * mm, "end": v(65, 59.5) * mm});
            skLineSegment(sketch, "E208.MirrorCS", {"start": v(91, 34.92) * mm, "end": v(93, 34.92) * mm});
            skLineSegment(sketch, "E209.MirrorCS", {"start": v(95, 34.92) * mm, "end": v(91, 34.92) * mm, "construction": true});
            skLineSegment(sketch, "E210.MirrorCS", {"start": v(91, 0) * mm, "end": v(91, 34.92) * mm});
            skLineSegment(sketch, "E211.MirrorCS", {"start": v(71, 60.5) * mm, "end": v(66, 60.5) * mm});
            skLineSegment(sketch, "E212.MirrorCS", {"start": v(90, 60.5) * mm, "end": v(85, 60.5) * mm});
            skLineSegment(sketch, "E213.MirrorCS", {"start": v(65, 0) * mm, "end": v(91, 0) * mm});
            skLineSegment(sketch, "E214.MirrorCS", {"start": v(65, 59.5) * mm, "end": v(65, 0) * mm});
            skLineSegment(sketch, "E215.MirrorCS", {"start": v(93, 34.92) * mm, "end": v(90, 60.5) * mm});
            skLineSegment(sketch, "E216.0", {"start": v(-95, 34.92) * mm, "end": v(-95, -35.08) * mm, "construction": true});
            skSolve(sketch);
        }
        {
            var Q0;
            Q0 = qSketchRegion(id + "F25", true);
            var Q1;
            Q1=sQuery(id+"F25.wireOp",EDGE,"E149");
            revolve(context, id + "F26", {"entities" : qUnion([Q0]), "axis" : qUnion([Q1]), "revolveType" : RevolveType.FULL});
        }
        {
            var Q0;
            Q0=makeQuery(id+"F5.opExtrude","SWEPT_BODY",BODY,{"disambiguationData":[OSD([sQuery(id+"F4.wireOp",EDGE,"E28.1"),sQuery(id+"F4.wireOp",EDGE,"E30.1"),sQuery(id+"F4.wireOp",EDGE,"E30.2"),sQuery(id+"F4.wireOp",EDGE,"E30.3"),sQuery(id+"F4.wireOp",EDGE,"E30.4"),sQuery(id+"F4.wireOp",EDGE,"E30.5"),sQuery(id+"F4.wireOp",EDGE,"E30.6"),sQuery(id+"F4.wireOp",EDGE,"E30.7")])]});
            var Q1;
            Q1=makeQuery(id+"F26.opRevolve","SWEPT_BODY",BODY,{"disambiguationData":[OSD([sQuery(id+"F25.wireOp",EDGE,"E168"),sQuery(id+"F25.wireOp",EDGE,"E169"),sQuery(id+"F25.wireOp",EDGE,"E170"),sQuery(id+"F25.wireOp",EDGE,"E171"),sQuery(id+"F25.wireOp",EDGE,"E172"),sQuery(id+"F25.wireOp",EDGE,"E173"),sQuery(id+"F25.wireOp",EDGE,"E174"),sQuery(id+"F25.wireOp",EDGE,"E175"),sQuery(id+"F25.wireOp",EDGE,"E176"),sQuery(id+"F25.wireOp",EDGE,"E177"),sQuery(id+"F25.wireOp",EDGE,"E178"),sQuery(id+"F25.wireOp",EDGE,"E179"),sQuery(id+"F25.wireOp",EDGE,"E180"),sQuery(id+"F25.wireOp",EDGE,"E181"),sQuery(id+"F25.wireOp",EDGE,"E182"),sQuery(id+"F25.wireOp",EDGE,"E183"),sQuery(id+"F25.wireOp",EDGE,"E184"),sQuery(id+"F25.wireOp",EDGE,"E185"),sQuery(id+"F25.wireOp",EDGE,"E186"),sQuery(id+"F25.wireOp",EDGE,"E187"),sQuery(id+"F25.wireOp",EDGE,"E188"),sQuery(id+"F25.wireOp",EDGE,"E190"),sQuery(id+"F25.wireOp",EDGE,"E191")])]});
            var Q2;
            Q2=makeQuery(id+"F26.opRevolve","SWEPT_BODY",BODY,{"disambiguationData":[OSD([sQuery(id+"F25.wireOp",EDGE,"E192.MirrorCS"),sQuery(id+"F25.wireOp",EDGE,"E193.MirrorCS"),sQuery(id+"F25.wireOp",EDGE,"E194.MirrorCS"),sQuery(id+"F25.wireOp",EDGE,"E195.MirrorCS"),sQuery(id+"F25.wireOp",EDGE,"E196.MirrorCS"),sQuery(id+"F25.wireOp",EDGE,"E197.MirrorCS"),sQuery(id+"F25.wireOp",EDGE,"E198.MirrorCS"),sQuery(id+"F25.wireOp",EDGE,"E199.MirrorCS"),sQuery(id+"F25.wireOp",EDGE,"E200.MirrorCS"),sQuery(id+"F25.wireOp",EDGE,"E201.MirrorCS"),sQuery(id+"F25.wireOp",EDGE,"E202.MirrorCS"),sQuery(id+"F25.wireOp",EDGE,"E203.MirrorCS"),sQuery(id+"F25.wireOp",EDGE,"E204.MirrorCS"),sQuery(id+"F25.wireOp",EDGE,"E205.MirrorCS"),sQuery(id+"F25.wireOp",EDGE,"E206.MirrorCS"),sQuery(id+"F25.wireOp",EDGE,"E207.MirrorCS"),sQuery(id+"F25.wireOp",EDGE,"E208.MirrorCS"),sQuery(id+"F25.wireOp",EDGE,"E210.MirrorCS"),sQuery(id+"F25.wireOp",EDGE,"E211.MirrorCS"),sQuery(id+"F25.wireOp",EDGE,"E212.MirrorCS"),sQuery(id+"F25.wireOp",EDGE,"E213.MirrorCS"),sQuery(id+"F25.wireOp",EDGE,"E214.MirrorCS"),sQuery(id+"F25.wireOp",EDGE,"E215.MirrorCS")])]});
            booleanBodies(context, id + "F27", {"operationType" : BooleanOperationType.SUBTRACTION, "tools" : qUnion([Q0]), "targets" : qUnion([Q1, Q2]), "keepTools" : true});
        }
    });
